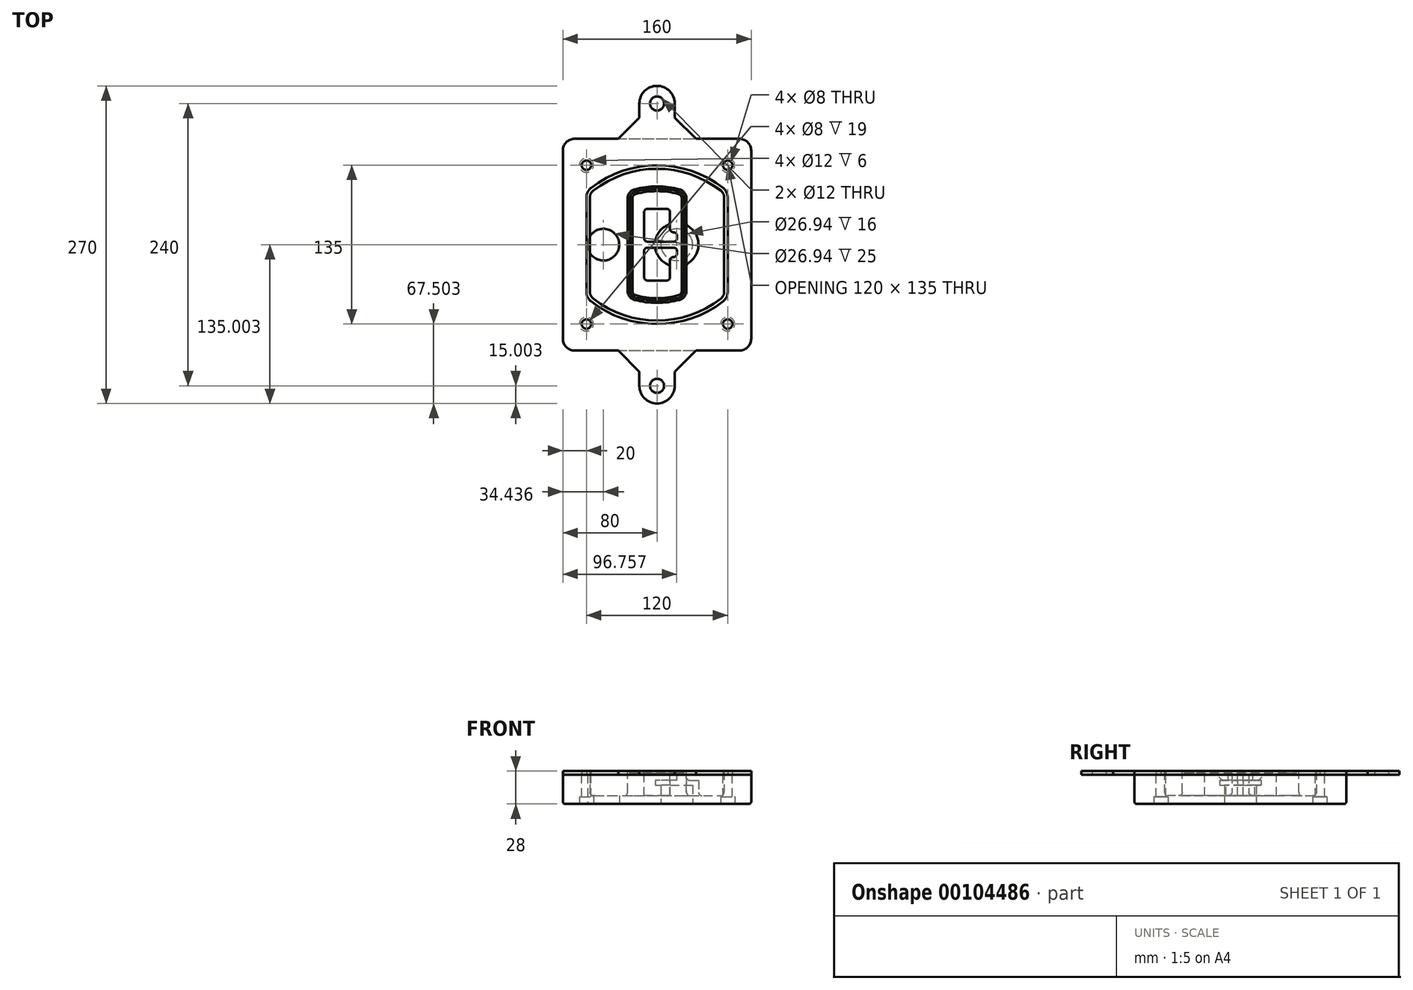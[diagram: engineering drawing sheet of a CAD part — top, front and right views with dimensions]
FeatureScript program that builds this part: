
annotation { "Feature Type Name" : "Feature", "Feature Type Description" : "" }
export const myFeature = defineFeature(function(context is Context, id is Id, definition is map)
    precondition{}
    {
        {
            var Q0;
            Q0=qCreatedBy(makeId("Top.planeOp"),FACE);
            var sketch = newSketch(context, id + "F0", { "sketchPlane" : qUnion([Q0])});
            skPoint(sketch, "E0.rect.middle", {"position": v(0, 0) * mm});
            skLineSegment(sketch, "E1.bottom", {"start": v(24.05, 28.38) * mm, "end": v(164.05, 28.38) * mm});
            skLineSegment(sketch, "E1.top", {"start": v(24.05, 208.38) * mm, "end": v(164.05, 208.38) * mm});
            skLineSegment(sketch, "E1.left", {"start": v(14.05, 38.38) * mm, "end": v(14.05, 198.38) * mm});
            skLineSegment(sketch, "E1.right", {"start": v(174.05, 38.38) * mm, "end": v(174.05, 198.38) * mm});
            skLineSegment(sketch, "E2", {"start": v(14.05, 208.38) * mm, "end": v(174.05, 28.38) * mm, "construction": true});
            skLineSegment(sketch, "E3", {"start": v(174.05, 208.38) * mm, "end": v(14.05, 28.38) * mm, "construction": true});
            skCircle(sketch, "E4", {"center": v(34.05, 185.88) * mm, "radius": 4 * mm});
            skCircle(sketch, "E5", {"center": v(154.05, 185.88) * mm, "radius": 4 * mm});
            skCircle(sketch, "E6", {"center": v(154.05, 50.88) * mm, "radius": 4 * mm});
            skCircle(sketch, "E7", {"center": v(34.05, 50.88) * mm, "radius": 4 * mm});
            skLineSegment(sketch, "E8", {"start": v(34.05, 185.88) * mm, "end": v(154.05, 185.88) * mm, "construction": true});
            skLineSegment(sketch, "E9", {"start": v(154.05, 185.88) * mm, "end": v(154.05, 50.88) * mm, "construction": true});
            skLineSegment(sketch, "E10", {"start": v(154.05, 50.88) * mm, "end": v(34.05, 50.88) * mm, "construction": true});
            skLineSegment(sketch, "E11", {"start": v(34.05, 50.88) * mm, "end": v(34.05, 185.88) * mm, "construction": true});
            skLineSegment(sketch, "E12", {"start": v(34.05, 158.68) * mm, "end": v(34.05, 78.09) * mm});
            skLineSegment(sketch, "E13", {"start": v(154.05, 158.68) * mm, "end": v(154.05, 78.09) * mm});
            skArc(sketch, "E14", {"start": v(150.2, 166.56) * mm, "mid": v(94.05, 185.88) * mm, "end": v(37.9, 166.56) * mm});
            skArc(sketch, "E15", {"start": v(37.9, 70.2) * mm, "mid": v(94.05, 50.88) * mm, "end": v(150.2, 70.2) * mm});
            skLineSegment(sketch, "E16", {"start": v(34.05, 118.38) * mm, "end": v(154.05, 118.38) * mm, "construction": true});
            skPoint(sketch, "E17.visualSharp", {"position": v(34.05, 73.38) * mm});
            skArc(sketch, "E17.filletArc", {"start": v(34.05, 78.09) * mm, "mid": v(35.06, 73.7) * mm, "end": v(37.9, 70.2) * mm});
            skPoint(sketch, "E18.visualSharp", {"position": v(34.05, 163.38) * mm});
            skArc(sketch, "E18.filletArc", {"start": v(37.9, 166.56) * mm, "mid": v(35.06, 163.06) * mm, "end": v(34.05, 158.68) * mm});
            skPoint(sketch, "E19.visualSharp", {"position": v(154.05, 163.38) * mm});
            skArc(sketch, "E19.filletArc", {"start": v(154.05, 158.68) * mm, "mid": v(153.04, 163.06) * mm, "end": v(150.2, 166.56) * mm});
            skPoint(sketch, "E20.visualSharp", {"position": v(154.05, 73.38) * mm});
            skArc(sketch, "E20.filletArc", {"start": v(150.2, 70.2) * mm, "mid": v(153.04, 73.7) * mm, "end": v(154.05, 78.09) * mm});
            skPoint(sketch, "E21.visualSharp", {"position": v(14.05, 208.38) * mm});
            skArc(sketch, "E21.filletArc", {"start": v(24.05, 208.38) * mm, "mid": v(16.98, 205.45) * mm, "end": v(14.05, 198.38) * mm});
            skPoint(sketch, "E22.visualSharp", {"position": v(174.05, 208.38) * mm});
            skArc(sketch, "E22.filletArc", {"start": v(174.05, 198.38) * mm, "mid": v(171.12, 205.45) * mm, "end": v(164.05, 208.38) * mm});
            skPoint(sketch, "E23.visualSharp", {"position": v(174.05, 28.38) * mm});
            skArc(sketch, "E23.filletArc", {"start": v(164.05, 28.38) * mm, "mid": v(171.12, 31.31) * mm, "end": v(174.05, 38.38) * mm});
            skPoint(sketch, "E24.visualSharp", {"position": v(14.05, 28.38) * mm});
            skArc(sketch, "E24.filletArc", {"start": v(14.05, 38.38) * mm, "mid": v(16.98, 31.31) * mm, "end": v(24.05, 28.38) * mm});
            skArc(sketch, "E25.0", {"start": v(151.05, 158.68) * mm, "mid": v(150.34, 161.75) * mm, "end": v(148.36, 164.2) * mm});
            skLineSegment(sketch, "E25.1", {"start": v(151.05, 158.68) * mm, "end": v(151.05, 78.09) * mm});
            skArc(sketch, "E25.2", {"start": v(148.36, 72.57) * mm, "mid": v(150.34, 75.02) * mm, "end": v(151.05, 78.09) * mm});
            skArc(sketch, "E25.3", {"start": v(39.74, 72.57) * mm, "mid": v(94.05, 53.88) * mm, "end": v(148.36, 72.57) * mm});
            skArc(sketch, "E25.4", {"start": v(37.05, 78.09) * mm, "mid": v(37.76, 75.02) * mm, "end": v(39.74, 72.57) * mm});
            skArc(sketch, "E25.5", {"start": v(148.36, 164.2) * mm, "mid": v(94.05, 182.88) * mm, "end": v(39.74, 164.2) * mm});
            skLineSegment(sketch, "E25.6", {"start": v(37.05, 158.68) * mm, "end": v(37.05, 78.09) * mm});
            skArc(sketch, "E25.7", {"start": v(39.74, 164.2) * mm, "mid": v(37.76, 161.75) * mm, "end": v(37.05, 158.68) * mm});
            skArc(sketch, "E26.0", {"start": v(35.43, 169.71) * mm, "mid": v(31.47, 164.82) * mm, "end": v(30.05, 158.68) * mm});
            skArc(sketch, "E26.1", {"start": v(152.67, 169.71) * mm, "mid": v(94.05, 189.88) * mm, "end": v(35.43, 169.71) * mm});
            skArc(sketch, "E26.2", {"start": v(158.05, 158.68) * mm, "mid": v(156.63, 164.82) * mm, "end": v(152.67, 169.71) * mm});
            skLineSegment(sketch, "E26.3", {"start": v(158.05, 158.68) * mm, "end": v(158.05, 78.09) * mm});
            skArc(sketch, "E26.4", {"start": v(152.67, 67.05) * mm, "mid": v(156.63, 71.95) * mm, "end": v(158.05, 78.09) * mm});
            skLineSegment(sketch, "E26.5", {"start": v(30.05, 158.68) * mm, "end": v(30.05, 78.09) * mm});
            skArc(sketch, "E26.6", {"start": v(35.43, 67.05) * mm, "mid": v(94.05, 46.88) * mm, "end": v(152.67, 67.05) * mm});
            skArc(sketch, "E26.7", {"start": v(30.05, 78.09) * mm, "mid": v(31.47, 71.95) * mm, "end": v(35.43, 67.05) * mm});
            skSolve(sketch);
        }
        {
            var Q0;
            Q0=makeQuery(id+"F0.imprint","IMPRINT",FACE,{"disambiguationData":[TD([[makeQuery(id+"F0.imprint","IMPRINT",EDGE,{"derivedFrom":sQuery(id+"F0.wireOp",EDGE,"E1.bottom")}),1.0]])]});
            var Q1;
            Q1=makeQuery(id+"F0.imprint","IMPRINT",FACE,{"disambiguationData":[TD([[makeQuery(id+"F0.imprint","IMPRINT",EDGE,{"derivedFrom":sQuery(id+"F0.wireOp",EDGE,"E12")}),1.0]])]});
            var Q2;
            Q2=makeQuery(id+"F0.imprint","IMPRINT",FACE,{"disambiguationData":[TD([[makeQuery(id+"F0.imprint","IMPRINT",EDGE,{"derivedFrom":sQuery(id+"F0.wireOp",EDGE,"E25.0")}),1.0]])]});
            var Q3;
            Q3=makeQuery(id+"F0.imprint","IMPRINT",FACE,{"disambiguationData":[TD([[makeQuery(id+"F0.imprint","IMPRINT",EDGE,{"derivedFrom":sQuery(id+"F0.wireOp",EDGE,"E12")}),-1.0]])]});
            extrude(context, id + "F1", {"entities" : qUnion([Q0, Q1, Q2, Q3]), "oppositeDirection" : true, "depth" : 25 * mm});
        }
        {
            var Q0;
            Q0=makeQuery(id+"F0.imprint","IMPRINT",FACE,{"disambiguationData":[TD([[makeQuery(id+"F0.imprint","IMPRINT",EDGE,{"derivedFrom":sQuery(id+"F0.wireOp",EDGE,"E12")}),1.0]])]});
            extrude(context, id + "F2", {"entities" : qUnion([Q0]), "operationType" : NewBodyOperationType.ADD, "depth" : 3 * mm});
        }
        {
            var Q0;
            Q0=makeQuery(id+"F0.imprint","IMPRINT",FACE,{"disambiguationData":[TD([[makeQuery(id+"F0.imprint","IMPRINT",EDGE,{"derivedFrom":sQuery(id+"F0.wireOp",EDGE,"E25.0")}),1.0]])]});
            extrude(context, id + "F3", {"entities" : qUnion([Q0]), "operationType" : NewBodyOperationType.REMOVE, "oppositeDirection" : true, "depth" : 18 * mm});
        }
        {
            var Q0;
            Q0=makeQuery(id+"F2.opExtrude","CAP_FACE",FACE,{"disambiguationData":[OSD([sQuery(id+"F0.wireOp",EDGE,"E12"),sQuery(id+"F0.wireOp",EDGE,"E13"),sQuery(id+"F0.wireOp",EDGE,"E14"),sQuery(id+"F0.wireOp",EDGE,"E15"),sQuery(id+"F0.wireOp",EDGE,"E17.filletArc"),sQuery(id+"F0.wireOp",EDGE,"E18.filletArc"),sQuery(id+"F0.wireOp",EDGE,"E19.filletArc"),sQuery(id+"F0.wireOp",EDGE,"E20.filletArc"),sQuery(id+"F0.wireOp",EDGE,"E25.0"),sQuery(id+"F0.wireOp",EDGE,"E25.1"),sQuery(id+"F0.wireOp",EDGE,"E25.2"),sQuery(id+"F0.wireOp",EDGE,"E25.3"),sQuery(id+"F0.wireOp",EDGE,"E25.4"),sQuery(id+"F0.wireOp",EDGE,"E25.5"),sQuery(id+"F0.wireOp",EDGE,"E25.6"),sQuery(id+"F0.wireOp",EDGE,"E25.7")])],"isStart":false});
            var sketch = newSketch(context, id + "F4", { "sketchPlane" : qUnion([Q0])});
            skArc(sketch, "E27.0", {"start": v(74.97, 71.41) * mm, "mid": v(94.05, 68.88) * mm, "end": v(113.13, 71.41) * mm});
            skArc(sketch, "E28.0", {"start": v(113.13, 165.35) * mm, "mid": v(94.05, 167.88) * mm, "end": v(74.97, 165.35) * mm});
            skLineSegment(sketch, "E29", {"start": v(69.05, 157.63) * mm, "end": v(69.05, 79.14) * mm});
            skLineSegment(sketch, "E30", {"start": v(119.05, 157.63) * mm, "end": v(119.05, 79.14) * mm});
            skLineSegment(sketch, "E31", {"start": v(69.05, 163.48) * mm, "end": v(119.05, 163.48) * mm, "construction": true});
            skLineSegment(sketch, "E32", {"start": v(69.05, 73.28) * mm, "end": v(119.05, 73.28) * mm, "construction": true});
            skPoint(sketch, "E33.visualSharp", {"position": v(69.05, 163.48) * mm});
            skArc(sketch, "E33.filletArc", {"start": v(74.97, 165.35) * mm, "mid": v(70.7, 162.5) * mm, "end": v(69.05, 157.63) * mm});
            skPoint(sketch, "E34.visualSharp", {"position": v(119.05, 163.48) * mm});
            skArc(sketch, "E34.filletArc", {"start": v(119.05, 157.63) * mm, "mid": v(117.4, 162.5) * mm, "end": v(113.13, 165.35) * mm});
            skPoint(sketch, "E35.visualSharp", {"position": v(119.05, 73.28) * mm});
            skArc(sketch, "E35.filletArc", {"start": v(113.13, 71.41) * mm, "mid": v(117.4, 74.27) * mm, "end": v(119.05, 79.14) * mm});
            skPoint(sketch, "E36.visualSharp", {"position": v(69.05, 73.28) * mm});
            skArc(sketch, "E36.filletArc", {"start": v(69.05, 79.14) * mm, "mid": v(70.7, 74.27) * mm, "end": v(74.97, 71.41) * mm});
            skArc(sketch, "E37.0", {"start": v(148.36, 164.2) * mm, "mid": v(94.05, 182.88) * mm, "end": v(39.74, 164.2) * mm});
            skArc(sketch, "E37.1", {"start": v(39.74, 164.2) * mm, "mid": v(37.76, 161.75) * mm, "end": v(37.05, 158.68) * mm});
            skLineSegment(sketch, "E37.2", {"start": v(37.05, 158.68) * mm, "end": v(37.05, 78.09) * mm});
            skArc(sketch, "E37.3", {"start": v(37.05, 78.09) * mm, "mid": v(37.76, 75.02) * mm, "end": v(39.74, 72.57) * mm});
            skArc(sketch, "E37.4", {"start": v(39.74, 72.57) * mm, "mid": v(94.05, 53.88) * mm, "end": v(148.36, 72.57) * mm});
            skArc(sketch, "E37.5", {"start": v(148.36, 72.57) * mm, "mid": v(150.34, 75.02) * mm, "end": v(151.05, 78.09) * mm});
            skLineSegment(sketch, "E37.6", {"start": v(151.05, 158.68) * mm, "end": v(151.05, 78.09) * mm});
            skArc(sketch, "E37.7", {"start": v(151.05, 158.68) * mm, "mid": v(150.34, 161.75) * mm, "end": v(148.36, 164.2) * mm});
            skLineSegment(sketch, "E38.0", {"start": v(117.05, 157.63) * mm, "end": v(117.05, 79.14) * mm});
            skArc(sketch, "E38.1", {"start": v(112.61, 73.34) * mm, "mid": v(115.81, 75.49) * mm, "end": v(117.05, 79.14) * mm});
            skArc(sketch, "E38.2", {"start": v(75.49, 73.34) * mm, "mid": v(94.05, 70.88) * mm, "end": v(112.61, 73.34) * mm});
            skArc(sketch, "E38.3", {"start": v(71.05, 79.14) * mm, "mid": v(72.29, 75.49) * mm, "end": v(75.49, 73.34) * mm});
            skLineSegment(sketch, "E38.4", {"start": v(71.05, 157.63) * mm, "end": v(71.05, 79.14) * mm});
            skArc(sketch, "E38.5", {"start": v(117.05, 157.63) * mm, "mid": v(115.81, 161.28) * mm, "end": v(112.61, 163.42) * mm});
            skArc(sketch, "E38.6", {"start": v(75.49, 163.42) * mm, "mid": v(72.29, 161.28) * mm, "end": v(71.05, 157.63) * mm});
            skArc(sketch, "E38.7", {"start": v(112.61, 163.42) * mm, "mid": v(94.05, 165.88) * mm, "end": v(75.49, 163.42) * mm});
            skArc(sketch, "E39.0", {"start": v(115.05, 157.63) * mm, "mid": v(114.23, 160.06) * mm, "end": v(112.1, 161.5) * mm});
            skLineSegment(sketch, "E39.1", {"start": v(115.05, 157.63) * mm, "end": v(115.05, 79.14) * mm});
            skArc(sketch, "E39.2", {"start": v(112.1, 75.27) * mm, "mid": v(114.23, 76.7) * mm, "end": v(115.05, 79.14) * mm});
            skArc(sketch, "E39.3", {"start": v(76, 75.27) * mm, "mid": v(94.05, 72.88) * mm, "end": v(112.1, 75.27) * mm});
            skArc(sketch, "E39.4", {"start": v(73.05, 79.14) * mm, "mid": v(73.87, 76.7) * mm, "end": v(76, 75.27) * mm});
            skArc(sketch, "E39.5", {"start": v(112.1, 161.5) * mm, "mid": v(94.05, 163.88) * mm, "end": v(76, 161.5) * mm});
            skLineSegment(sketch, "E39.6", {"start": v(73.05, 157.63) * mm, "end": v(73.05, 79.14) * mm});
            skArc(sketch, "E39.7", {"start": v(76, 161.5) * mm, "mid": v(73.87, 160.06) * mm, "end": v(73.05, 157.63) * mm});
            skLineSegment(sketch, "E40", {"start": v(69.05, 118.38) * mm, "end": v(119.05, 118.38) * mm, "construction": true});
            skLineSegment(sketch, "E41", {"start": v(83.05, 123.88) * mm, "end": v(83.05, 145.88) * mm});
            skLineSegment(sketch, "E42", {"start": v(86.05, 148.88) * mm, "end": v(102.05, 148.88) * mm});
            skLineSegment(sketch, "E43", {"start": v(105.05, 145.88) * mm, "end": v(105.05, 131.88) * mm});
            skLineSegment(sketch, "E44", {"start": v(108.05, 128.88) * mm, "end": v(108.05, 128.88) * mm});
            skLineSegment(sketch, "E45", {"start": v(111.05, 125.88) * mm, "end": v(111.05, 123.88) * mm});
            skLineSegment(sketch, "E46", {"start": v(108.05, 120.88) * mm, "end": v(86.05, 120.88) * mm});
            skPoint(sketch, "E47.visualSharp", {"position": v(83.05, 148.88) * mm});
            skArc(sketch, "E47.filletArc", {"start": v(86.05, 148.88) * mm, "mid": v(83.93, 148) * mm, "end": v(83.05, 145.88) * mm});
            skPoint(sketch, "E48.visualSharp", {"position": v(105.05, 148.88) * mm});
            skArc(sketch, "E48.filletArc", {"start": v(105.05, 145.88) * mm, "mid": v(104.17, 148) * mm, "end": v(102.05, 148.88) * mm});
            skPoint(sketch, "E49.visualSharp", {"position": v(105.05, 128.88) * mm});
            skArc(sketch, "E49.filletArc", {"start": v(105.05, 131.88) * mm, "mid": v(105.93, 129.76) * mm, "end": v(108.05, 128.88) * mm});
            skPoint(sketch, "E50.visualSharp", {"position": v(111.05, 128.88) * mm});
            skArc(sketch, "E50.filletArc", {"start": v(111.05, 125.88) * mm, "mid": v(110.17, 128) * mm, "end": v(108.05, 128.88) * mm});
            skPoint(sketch, "E51.visualSharp", {"position": v(111.05, 120.88) * mm});
            skArc(sketch, "E51.filletArc", {"start": v(108.05, 120.88) * mm, "mid": v(110.17, 121.76) * mm, "end": v(111.05, 123.88) * mm});
            skPoint(sketch, "E52.visualSharp", {"position": v(83.05, 120.88) * mm});
            skArc(sketch, "E52.filletArc", {"start": v(83.05, 123.88) * mm, "mid": v(83.93, 121.76) * mm, "end": v(86.05, 120.88) * mm});
            skLineSegment(sketch, "E53.0.MirrorCS", {"start": v(108.05, 115.88) * mm, "end": v(86.05, 115.88) * mm});
            skArc(sketch, "E54.0.MirrorCS", {"start": v(83.05, 112.88) * mm, "mid": v(83.93, 115) * mm, "end": v(86.05, 115.88) * mm});
            skLineSegment(sketch, "E55.0.MirrorCS", {"start": v(83.05, 112.88) * mm, "end": v(83.05, 90.88) * mm});
            skArc(sketch, "E56.0.MirrorCS", {"start": v(86.05, 87.88) * mm, "mid": v(83.93, 88.76) * mm, "end": v(83.05, 90.88) * mm});
            skLineSegment(sketch, "E57.0.MirrorCS", {"start": v(86.05, 87.88) * mm, "end": v(102.05, 87.88) * mm});
            skArc(sketch, "E58.0.MirrorCS", {"start": v(105.05, 90.88) * mm, "mid": v(104.17, 88.76) * mm, "end": v(102.05, 87.88) * mm});
            skLineSegment(sketch, "E59.0.MirrorCS", {"start": v(105.05, 90.88) * mm, "end": v(105.05, 104.88) * mm});
            skArc(sketch, "E60.0.MirrorCS", {"start": v(105.05, 104.88) * mm, "mid": v(105.93, 107) * mm, "end": v(108.05, 107.88) * mm});
            skArc(sketch, "E61.0.MirrorCS", {"start": v(111.05, 110.88) * mm, "mid": v(110.17, 108.76) * mm, "end": v(108.05, 107.88) * mm});
            skLineSegment(sketch, "E62.0.MirrorCS", {"start": v(111.05, 110.88) * mm, "end": v(111.05, 112.88) * mm});
            skArc(sketch, "E63.0.MirrorCS", {"start": v(108.05, 115.88) * mm, "mid": v(110.17, 115) * mm, "end": v(111.05, 112.88) * mm});
            skSolve(sketch);
        }
        {
            var Q0;
            Q0=makeQuery(id+"F4.imprint","IMPRINT",FACE,{"disambiguationData":[TD([[makeQuery(id+"F4.imprint","IMPRINT",EDGE,{"derivedFrom":sQuery(id+"F4.wireOp",EDGE,"E27.0")}),1.0]])]});
            var Q1;
            Q1=makeQuery(id+"F4.imprint","IMPRINT",FACE,{"disambiguationData":[TD([[makeQuery(id+"F4.imprint","IMPRINT",EDGE,{"derivedFrom":sQuery(id+"F4.wireOp",EDGE,"E38.0")}),-1.0]])]});
            var Q2;
            Q2=makeQuery(id+"F4.imprint","IMPRINT",FACE,{"disambiguationData":[TD([[makeQuery(id+"F4.imprint","IMPRINT",EDGE,{"derivedFrom":sQuery(id+"F4.wireOp",EDGE,"E39.0")}),1.0]])]});
            extrude(context, id + "F5", {"entities" : qUnion([Q0, Q1, Q2]), "operationType" : NewBodyOperationType.ADD, "endBound" : BoundingType.UP_TO_NEXT, "oppositeDirection" : true, "depth" : 25 * mm});
        }
        {
            var Q0;
            Q0=makeQuery(id+"F4.imprint","IMPRINT",FACE,{"disambiguationData":[TD([[makeQuery(id+"F4.imprint","IMPRINT",EDGE,{"derivedFrom":sQuery(id+"F4.wireOp",EDGE,"E38.0")}),-1.0]])]});
            extrude(context, id + "F6", {"entities" : qUnion([Q0]), "operationType" : NewBodyOperationType.REMOVE, "oppositeDirection" : true, "depth" : 2 * mm});
        }
        {
            var Q0;
            Q0=makeQuery(id+"F1.opExtrude","CAP_FACE",FACE,{"disambiguationData":[OSD([sQuery(id+"F0.wireOp",EDGE,"E1.bottom"),sQuery(id+"F0.wireOp",EDGE,"E1.top"),sQuery(id+"F0.wireOp",EDGE,"E1.left"),sQuery(id+"F0.wireOp",EDGE,"E1.right"),sQuery(id+"F0.wireOp",EDGE,"E4"),sQuery(id+"F0.wireOp",EDGE,"E5"),sQuery(id+"F0.wireOp",EDGE,"E6"),sQuery(id+"F0.wireOp",EDGE,"E7"),sQuery(id+"F0.wireOp",EDGE,"E21.filletArc"),sQuery(id+"F0.wireOp",EDGE,"E22.filletArc"),sQuery(id+"F0.wireOp",EDGE,"E23.filletArc"),sQuery(id+"F0.wireOp",EDGE,"E24.filletArc")])],"isStart":false});
            var sketch = newSketch(context, id + "F7", { "sketchPlane" : qUnion([Q0])});
            skCircle(sketch, "E64", {"center": v(110.8, -118.38) * mm, "radius": 13.47 * mm});
            skCircle(sketch, "E65", {"center": v(48.49, -118.38) * mm, "radius": 13.47 * mm});
            skLineSegment(sketch, "E66", {"start": v(174.05, -118.38) * mm, "end": v(14.05, -118.38) * mm});
            skCircle(sketch, "E67", {"center": v(110.8, -118.38) * mm, "radius": 18.47 * mm});
            skCircle(sketch, "E68", {"center": v(154.05, -185.88) * mm, "radius": 6 * mm});
            skCircle(sketch, "E69", {"center": v(34.05, -185.88) * mm, "radius": 6 * mm});
            skCircle(sketch, "E70", {"center": v(34.05, -50.88) * mm, "radius": 6 * mm});
            skCircle(sketch, "E71", {"center": v(154.05, -50.88) * mm, "radius": 6 * mm});
            skSolve(sketch);
        }
        {
            var Q0;
            {var subQ1=sQuery(id+"F7.wireOp",EDGE,"E66");var subQ4=sQuery(id+"F7.wireOp",EDGE,"E64");var subQ6=makeQuery(id+"F7.imprint","INTERSECT",VERTEX,{"disambiguationData":[OD(0.0)],"derivedFrom":[subQ4,subQ1]});Q0=makeQuery(id+"F7.imprint","IMPRINT",FACE,{"disambiguationData":[TD([[makeQuery(id+"F7.imprint","IMPRINT",EDGE,{"disambiguationData":[TD([[subQ6,-1.0]])],"derivedFrom":subQ4}),-1.0]])]});}
            var Q1;
            {var subQ0=sQuery(id+"F7.wireOp",EDGE,"E66");var subQ1=sQuery(id+"F7.wireOp",EDGE,"E64");var subQ3=makeQuery(id+"F7.imprint","INTERSECT",VERTEX,{"disambiguationData":[OD(0.0)],"derivedFrom":[subQ1,subQ0]});Q1=makeQuery(id+"F7.imprint","IMPRINT",FACE,{"disambiguationData":[TD([[makeQuery(id+"F7.imprint","IMPRINT",EDGE,{"disambiguationData":[TD([[subQ3,-1.0]])],"derivedFrom":subQ1}),1.0]])]});}
            var Q2;
            {var subQ0=sQuery(id+"F7.wireOp",EDGE,"E66");var subQ1=sQuery(id+"F7.wireOp",EDGE,"E64");var subQ3=makeQuery(id+"F7.imprint","INTERSECT",VERTEX,{"disambiguationData":[OD(0.0)],"derivedFrom":[subQ1,subQ0]});Q2=makeQuery(id+"F7.imprint","IMPRINT",FACE,{"disambiguationData":[TD([[makeQuery(id+"F7.imprint","IMPRINT",EDGE,{"disambiguationData":[TD([[subQ3,1.0]])],"derivedFrom":subQ1}),1.0]])]});}
            var Q3;
            {var subQ1=sQuery(id+"F7.wireOp",EDGE,"E66");var subQ4=sQuery(id+"F7.wireOp",EDGE,"E64");var subQ6=makeQuery(id+"F7.imprint","INTERSECT",VERTEX,{"disambiguationData":[OD(0.0)],"derivedFrom":[subQ4,subQ1]});Q3=makeQuery(id+"F7.imprint","IMPRINT",FACE,{"disambiguationData":[TD([[makeQuery(id+"F7.imprint","IMPRINT",EDGE,{"disambiguationData":[TD([[subQ6,1.0]])],"derivedFrom":subQ4}),-1.0]])]});}
            extrude(context, id + "F8", {"entities" : qUnion([Q0, Q1, Q2, Q3]), "operationType" : NewBodyOperationType.ADD, "oppositeDirection" : true, "depth" : 20 * mm});
        }
        {
            var Q0;
            {var subQ0=sQuery(id+"F7.wireOp",EDGE,"E66");var subQ1=sQuery(id+"F7.wireOp",EDGE,"E64");var subQ3=makeQuery(id+"F7.imprint","INTERSECT",VERTEX,{"disambiguationData":[OD(0.0)],"derivedFrom":[subQ1,subQ0]});Q0=makeQuery(id+"F7.imprint","IMPRINT",FACE,{"disambiguationData":[TD([[makeQuery(id+"F7.imprint","IMPRINT",EDGE,{"disambiguationData":[TD([[subQ3,-1.0]])],"derivedFrom":subQ1}),1.0]])]});}
            var Q1;
            {var subQ0=sQuery(id+"F7.wireOp",EDGE,"E66");var subQ1=sQuery(id+"F7.wireOp",EDGE,"E64");var subQ3=makeQuery(id+"F7.imprint","INTERSECT",VERTEX,{"disambiguationData":[OD(0.0)],"derivedFrom":[subQ1,subQ0]});Q1=makeQuery(id+"F7.imprint","IMPRINT",FACE,{"disambiguationData":[TD([[makeQuery(id+"F7.imprint","IMPRINT",EDGE,{"disambiguationData":[TD([[subQ3,1.0]])],"derivedFrom":subQ1}),1.0]])]});}
            extrude(context, id + "F9", {"entities" : qUnion([Q0, Q1]), "operationType" : NewBodyOperationType.REMOVE, "oppositeDirection" : true, "depth" : 16 * mm});
        }
        {
            var Q0;
            {var subQ0=sQuery(id+"F7.wireOp",EDGE,"E66");var subQ1=sQuery(id+"F7.wireOp",EDGE,"E65");var subQ3=makeQuery(id+"F7.imprint","INTERSECT",VERTEX,{"disambiguationData":[OD(0.0)],"derivedFrom":[subQ1,subQ0]});Q0=makeQuery(id+"F7.imprint","IMPRINT",FACE,{"disambiguationData":[TD([[makeQuery(id+"F7.imprint","IMPRINT",EDGE,{"disambiguationData":[TD([[subQ3,-1.0]])],"derivedFrom":subQ1}),1.0]])]});}
            var Q1;
            {var subQ0=sQuery(id+"F7.wireOp",EDGE,"E66");var subQ1=sQuery(id+"F7.wireOp",EDGE,"E65");var subQ3=makeQuery(id+"F7.imprint","INTERSECT",VERTEX,{"disambiguationData":[OD(0.0)],"derivedFrom":[subQ1,subQ0]});Q1=makeQuery(id+"F7.imprint","IMPRINT",FACE,{"disambiguationData":[TD([[makeQuery(id+"F7.imprint","IMPRINT",EDGE,{"disambiguationData":[TD([[subQ3,1.0]])],"derivedFrom":subQ1}),1.0]])]});}
            extrude(context, id + "F10", {"entities" : qUnion([Q0, Q1]), "operationType" : NewBodyOperationType.REMOVE, "oppositeDirection" : true, "depth" : 25 * mm});
        }
        {
            var Q0;
            Q0=makeQuery(id+"F7.imprint","IMPRINT",FACE,{"disambiguationData":[TD([[makeQuery(id+"F7.imprint","IMPRINT",EDGE,{"derivedFrom":sQuery(id+"F7.wireOp",EDGE,"E68")}),1.0]])]});
            var Q1;
            Q1=makeQuery(id+"F7.imprint","IMPRINT",FACE,{"disambiguationData":[TD([[makeQuery(id+"F7.imprint","IMPRINT",EDGE,{"derivedFrom":makeQuery(id+"F1.opExtrude","CAP_EDGE",EDGE,{"disambiguationData":[OSD([sQuery(id+"F0.wireOp",EDGE,"E5")])],"isStart":false})}),-1.0]])]});
            var Q2;
            Q2=makeQuery(id+"F7.imprint","IMPRINT",FACE,{"disambiguationData":[TD([[makeQuery(id+"F7.imprint","IMPRINT",EDGE,{"derivedFrom":sQuery(id+"F7.wireOp",EDGE,"E69")}),1.0]])]});
            var Q3;
            Q3=makeQuery(id+"F7.imprint","IMPRINT",FACE,{"disambiguationData":[TD([[makeQuery(id+"F7.imprint","IMPRINT",EDGE,{"derivedFrom":makeQuery(id+"F1.opExtrude","CAP_EDGE",EDGE,{"disambiguationData":[OSD([sQuery(id+"F0.wireOp",EDGE,"E4")])],"isStart":false})}),-1.0]])]});
            var Q4;
            Q4=makeQuery(id+"F7.imprint","IMPRINT",FACE,{"disambiguationData":[TD([[makeQuery(id+"F7.imprint","IMPRINT",EDGE,{"derivedFrom":sQuery(id+"F7.wireOp",EDGE,"E70")}),1.0]])]});
            var Q5;
            Q5=makeQuery(id+"F7.imprint","IMPRINT",FACE,{"disambiguationData":[TD([[makeQuery(id+"F7.imprint","IMPRINT",EDGE,{"derivedFrom":makeQuery(id+"F1.opExtrude","CAP_EDGE",EDGE,{"disambiguationData":[OSD([sQuery(id+"F0.wireOp",EDGE,"E7")])],"isStart":false})}),-1.0]])]});
            var Q6;
            Q6=makeQuery(id+"F7.imprint","IMPRINT",FACE,{"disambiguationData":[TD([[makeQuery(id+"F7.imprint","IMPRINT",EDGE,{"derivedFrom":sQuery(id+"F7.wireOp",EDGE,"E71")}),1.0]])]});
            var Q7;
            Q7=makeQuery(id+"F7.imprint","IMPRINT",FACE,{"disambiguationData":[TD([[makeQuery(id+"F7.imprint","IMPRINT",EDGE,{"derivedFrom":makeQuery(id+"F1.opExtrude","CAP_EDGE",EDGE,{"disambiguationData":[OSD([sQuery(id+"F0.wireOp",EDGE,"E6")])],"isStart":false})}),-1.0]])]});
            extrude(context, id + "F11", {"entities" : qUnion([Q0, Q1, Q2, Q3, Q4, Q5, Q6, Q7]), "operationType" : NewBodyOperationType.REMOVE, "oppositeDirection" : true, "depth" : 6 * mm});
        }
        {
            var Q0;
            Q0=makeQuery(id+"F9.boolean.opBoolean","COPY",FACE,{"derivedFrom":makeQuery(id+"F9.opExtrude","CAP_FACE",FACE,{"disambiguationData":[OSD([sQuery(id+"F7.wireOp",EDGE,"E64")])],"isStart":false})});
            var sketch = newSketch(context, id + "F12", { "sketchPlane" : qUnion([Q0])});
            skArc(sketch, "E72.0", {"start": v(105.05, -100.83) * mm, "mid": v(96.62, -106.56) * mm, "end": v(92.5, -115.88) * mm});
            skArc(sketch, "E72.1", {"start": v(92.5, -120.88) * mm, "mid": v(96.62, -130.2) * mm, "end": v(105.05, -135.93) * mm});
            skLineSegment(sketch, "E73", {"start": v(92.5, -120.88) * mm, "end": v(108.05, -120.88) * mm});
            skLineSegment(sketch, "E74.0", {"start": v(108.05, -115.88) * mm, "end": v(92.5, -115.88) * mm});
            skArc(sketch, "E74.1", {"start": v(108.05, -115.88) * mm, "mid": v(110.17, -115) * mm, "end": v(111.05, -112.88) * mm});
            skLineSegment(sketch, "E74.2", {"start": v(111.05, -110.88) * mm, "end": v(111.05, -112.88) * mm});
            skArc(sketch, "E74.3", {"start": v(111.05, -110.88) * mm, "mid": v(110.17, -108.76) * mm, "end": v(108.05, -107.88) * mm});
            skArc(sketch, "E74.4", {"start": v(105.05, -104.88) * mm, "mid": v(105.93, -107) * mm, "end": v(108.05, -107.88) * mm});
            skLineSegment(sketch, "E74.5", {"start": v(105.05, -100.83) * mm, "end": v(105.05, -104.88) * mm});
            skLineSegment(sketch, "E74.7", {"start": v(108.05, -120.88) * mm, "end": v(92.5, -120.88) * mm});
            skArc(sketch, "E74.8", {"start": v(108.05, -120.88) * mm, "mid": v(110.17, -121.76) * mm, "end": v(111.05, -123.88) * mm});
            skLineSegment(sketch, "E74.9", {"start": v(111.05, -125.88) * mm, "end": v(111.05, -123.88) * mm});
            skArc(sketch, "E74.10", {"start": v(111.05, -125.88) * mm, "mid": v(110.17, -128) * mm, "end": v(108.05, -128.88) * mm});
            skArc(sketch, "E74.11", {"start": v(105.05, -131.88) * mm, "mid": v(105.93, -129.76) * mm, "end": v(108.05, -128.88) * mm});
            skLineSegment(sketch, "E74.12", {"start": v(105.05, -135.93) * mm, "end": v(105.05, -131.88) * mm});
            skPoint(sketch, "E75.orphan", {"position": v(105.05, -145.88) * mm});
            skPoint(sketch, "E76.orphan", {"position": v(86.05, -120.88) * mm});
            skPoint(sketch, "E77.orphan", {"position": v(86.05, -115.88) * mm});
            skPoint(sketch, "E78.orphan", {"position": v(105.05, -90.88) * mm});
            skSolve(sketch);
        }
        {
            var Q0;
            {var subQ7=sQuery(id+"F12.wireOp",EDGE,"E72.0");var subQ14=sQuery(id+"F12.wireOp",EDGE,"E72.1");var subQ16=sQuery(id+"F12.wireOp",EDGE,"E74.1");var subQ18=sQuery(id+"F12.wireOp",EDGE,"E74.8");Q0=qUnion([makeQuery(id+"F12.imprint","IMPRINT",FACE,{"disambiguationData":[TD([[makeQuery(id+"F12.imprint","IMPRINT",EDGE,{"derivedFrom":subQ7}),1.0]])]}),makeQuery(id+"F12.imprint","IMPRINT",FACE,{"disambiguationData":[TD([[makeQuery(id+"F12.imprint","IMPRINT",EDGE,{"derivedFrom":subQ14}),1.0]])]}),makeQuery(id+"F12.imprint","IMPRINT",FACE,{"disambiguationData":[TD([[makeQuery(id+"F12.imprint","IMPRINT",EDGE,{"derivedFrom":subQ16}),1.0]])]}),makeQuery(id+"F12.imprint","IMPRINT",FACE,{"disambiguationData":[TD([[makeQuery(id+"F12.imprint","IMPRINT",EDGE,{"derivedFrom":subQ18}),-1.0]])]})]);}
            var Q1;
            Q1=makeQuery(id+"F5.boolean.opBoolean","SPLIT",FACE,{"disambiguationData":[TD([makeQuery(id+"F5.opExtrude","SWEPT_FACE",FACE,{"disambiguationData":[OSD([sQuery(id+"F4.wireOp",EDGE,"E41")])]})])],"derivedFrom":makeQuery(id+"F3.boolean.opBoolean","COPY",FACE,{"derivedFrom":makeQuery(id+"F3.opExtrude","CAP_FACE",FACE,{"disambiguationData":[OSD([sQuery(id+"F0.wireOp",EDGE,"E25.0"),sQuery(id+"F0.wireOp",EDGE,"E25.1"),sQuery(id+"F0.wireOp",EDGE,"E25.2"),sQuery(id+"F0.wireOp",EDGE,"E25.3"),sQuery(id+"F0.wireOp",EDGE,"E25.4"),sQuery(id+"F0.wireOp",EDGE,"E25.5"),sQuery(id+"F0.wireOp",EDGE,"E25.6"),sQuery(id+"F0.wireOp",EDGE,"E25.7")])],"isStart":false})})});
            extrude(context, id + "F13", {"entities" : qUnion([Q0]), "operationType" : NewBodyOperationType.REMOVE, "endBound" : BoundingType.UP_TO_SURFACE, "endBoundEntityFace" : qUnion([Q1]), "depth" : 25 * mm});
        }
        {
            var Q0;
            Q0=makeQuery(id+"F3.boolean.opBoolean","COPY",EDGE,{"derivedFrom":makeQuery(id+"F3.opExtrude","CAP_EDGE",EDGE,{"disambiguationData":[OSD([sQuery(id+"F0.wireOp",EDGE,"E25.6")])],"isStart":false})});
            var Q1;
            Q1=makeQuery(id+"F8.boolean.opBoolean","INTERSECT",EDGE,{"derivedFrom":[makeQuery(id+"F5.opExtrude","SWEPT_FACE",FACE,{"disambiguationData":[OSD([sQuery(id+"F4.wireOp",EDGE,"E30")])]}),makeQuery(id+"F8.opExtrude","CAP_FACE",FACE,{"disambiguationData":[OSD([sQuery(id+"F7.wireOp",EDGE,"E67")])],"isStart":false})]});
            var Q2;
            Q2=makeQuery(id+"F8.boolean.opBoolean","INTERSECT",EDGE,{"disambiguationData":[OD(1.0)],"derivedFrom":[makeQuery(id+"F5.opExtrude","SWEPT_FACE",FACE,{"disambiguationData":[OSD([sQuery(id+"F4.wireOp",EDGE,"E30")])]}),makeQuery(id+"F8.opExtrude","SWEPT_FACE",FACE,{"disambiguationData":[OSD([sQuery(id+"F7.wireOp",EDGE,"E67")])]})]});
            var Q3;
            {var subQ0=sQuery(id+"F4.wireOp",EDGE,"E30");Q3=makeQuery(id+"F8.boolean.opBoolean","SPLIT",EDGE,{"disambiguationData":[TD([makeQuery(id+"F5.opExtrude","SWEPT_FACE",FACE,{"disambiguationData":[OSD([sQuery(id+"F4.wireOp",EDGE,"E35.filletArc")])]})])],"derivedFrom":makeQuery(id+"F5.opExtrude","CAP_EDGE",EDGE,{"disambiguationData":[OSD([subQ0])],"isStart":false})});}
            var Q4;
            {var subQ0=sQuery(id+"F0.wireOp",EDGE,"E25.7");var subQ1=sQuery(id+"F0.wireOp",EDGE,"E25.1");var subQ2=sQuery(id+"F0.wireOp",EDGE,"E25.6");var subQ3=sQuery(id+"F0.wireOp",EDGE,"E25.5");var subQ4=sQuery(id+"F0.wireOp",EDGE,"E25.4");var subQ5=sQuery(id+"F0.wireOp",EDGE,"E25.0");var subQ6=sQuery(id+"F0.wireOp",EDGE,"E25.2");var subQ7=sQuery(id+"F0.wireOp",EDGE,"E25.3");Q4=makeQuery(id+"F8.boolean.opBoolean","INTERSECT",EDGE,{"derivedFrom":[makeQuery(id+"F5.boolean.opBoolean","SPLIT",FACE,{"disambiguationData":[TD([makeQuery(id+"F2.opExtrude","SWEPT_FACE",FACE,{"disambiguationData":[OSD([subQ5])]})])],"derivedFrom":makeQuery(id+"F3.boolean.opBoolean","COPY",FACE,{"derivedFrom":makeQuery(id+"F3.opExtrude","CAP_FACE",FACE,{"disambiguationData":[OSD([subQ5,subQ1,subQ6,subQ7,subQ4,subQ3,subQ2,subQ0])],"isStart":false})})}),makeQuery(id+"F8.opExtrude","SWEPT_FACE",FACE,{"disambiguationData":[OSD([sQuery(id+"F7.wireOp",EDGE,"E67")])]})]});}
            var Q5;
            Q5=makeQuery(id+"F8.boolean.opBoolean","INTERSECT",EDGE,{"disambiguationData":[OD(0.0)],"derivedFrom":[makeQuery(id+"F5.opExtrude","SWEPT_FACE",FACE,{"disambiguationData":[OSD([sQuery(id+"F4.wireOp",EDGE,"E30")])]}),makeQuery(id+"F8.opExtrude","SWEPT_FACE",FACE,{"disambiguationData":[OSD([sQuery(id+"F7.wireOp",EDGE,"E67")])]})]});
            fillet(context, id + "F14", {"entities" : qUnion([Q0, Q1, Q2, Q3, Q4, Q5]), "radius" : 3 * mm, "tangentPropagation" : true, "allowEdgeOverflow" : false});
        }
        {
            var Q0;
            Q0=makeQuery(id+"F1.opExtrude","CAP_EDGE",EDGE,{"disambiguationData":[OSD([sQuery(id+"F0.wireOp",EDGE,"E1.bottom")])],"isStart":false});
            fillet(context, id + "F15", {"entities" : qUnion([Q0]), "radius" : 2 * mm, "tangentPropagation" : true, "allowEdgeOverflow" : false});
        }
        {
            var Q0;
            Q0=qCreatedBy(makeId("Top.planeOp"),FACE);
            var sketch = newSketch(context, id + "F16", { "sketchPlane" : qUnion([Q0])});
            skLineSegment(sketch, "E79.0", {"start": v(14.05, 38.38) * mm, "end": v(14.05, 198.38) * mm});
            skArc(sketch, "E79.1", {"start": v(24.05, 208.38) * mm, "mid": v(16.98, 205.45) * mm, "end": v(14.05, 198.38) * mm});
            skCircle(sketch, "E79.2", {"center": v(34.05, 185.88) * mm, "radius": 4 * mm});
            skArc(sketch, "E79.3", {"start": v(37.9, 166.56) * mm, "mid": v(35.06, 163.06) * mm, "end": v(34.05, 158.68) * mm});
            skLineSegment(sketch, "E79.4", {"start": v(34.05, 158.68) * mm, "end": v(34.05, 78.09) * mm});
            skArc(sketch, "E79.5", {"start": v(150.2, 166.56) * mm, "mid": v(94.05, 185.88) * mm, "end": v(37.9, 166.56) * mm});
            skLineSegment(sketch, "E79.6", {"start": v(24.05, 208.38) * mm, "end": v(164.05, 208.38) * mm});
            skArc(sketch, "E79.7", {"start": v(174.05, 198.38) * mm, "mid": v(171.12, 205.45) * mm, "end": v(164.05, 208.38) * mm});
            skCircle(sketch, "E79.8", {"center": v(154.05, 185.88) * mm, "radius": 4 * mm});
            skArc(sketch, "E79.9", {"start": v(154.05, 158.68) * mm, "mid": v(153.04, 163.06) * mm, "end": v(150.2, 166.56) * mm});
            skLineSegment(sketch, "E79.10", {"start": v(154.05, 158.68) * mm, "end": v(154.05, 78.09) * mm});
            skLineSegment(sketch, "E79.11", {"start": v(174.05, 38.38) * mm, "end": v(174.05, 198.38) * mm});
            skArc(sketch, "E79.12", {"start": v(164.05, 28.38) * mm, "mid": v(171.12, 31.31) * mm, "end": v(174.05, 38.38) * mm});
            skCircle(sketch, "E79.13", {"center": v(154.05, 50.88) * mm, "radius": 4 * mm});
            skArc(sketch, "E79.14", {"start": v(150.2, 70.2) * mm, "mid": v(153.04, 73.7) * mm, "end": v(154.05, 78.09) * mm});
            skArc(sketch, "E79.15", {"start": v(37.9, 70.2) * mm, "mid": v(94.05, 50.88) * mm, "end": v(150.2, 70.2) * mm});
            skLineSegment(sketch, "E79.16", {"start": v(24.05, 28.38) * mm, "end": v(164.05, 28.38) * mm});
            skArc(sketch, "E79.17", {"start": v(14.05, 38.38) * mm, "mid": v(16.98, 31.31) * mm, "end": v(24.05, 28.38) * mm});
            skCircle(sketch, "E79.18", {"center": v(34.05, 50.88) * mm, "radius": 4 * mm});
            skArc(sketch, "E79.19", {"start": v(34.05, 78.09) * mm, "mid": v(35.06, 73.7) * mm, "end": v(37.9, 70.2) * mm});
            skLineSegment(sketch, "E80", {"start": v(94.05, 208.38) * mm, "end": v(94.05, 238.38) * mm, "construction": true});
            skLineSegment(sketch, "E81", {"start": v(61.05, 208.38) * mm, "end": v(79.05, 226.38) * mm});
            skLineSegment(sketch, "E82", {"start": v(79.05, 226.38) * mm, "end": v(79.05, 238.38) * mm});
            skLineSegment(sketch, "E83", {"start": v(127.05, 208.38) * mm, "end": v(109.05, 226.38) * mm});
            skLineSegment(sketch, "E84", {"start": v(109.05, 226.38) * mm, "end": v(109.05, 238.38) * mm});
            skCircle(sketch, "E85", {"center": v(94.05, 238.38) * mm, "radius": 6 * mm});
            skArc(sketch, "E86", {"start": v(109.05, 238.38) * mm, "mid": v(94.05, 253.38) * mm, "end": v(79.05, 238.38) * mm});
            skLineSegment(sketch, "E87", {"start": v(14.05, 118.38) * mm, "end": v(174.05, 118.38) * mm, "construction": true});
            skArc(sketch, "E88.MirrorCS", {"start": v(109.05, -1.62) * mm, "mid": v(94.05, -16.62) * mm, "end": v(79.05, -1.62) * mm});
            skLineSegment(sketch, "E89.MirrorCS", {"start": v(109.05, 10.38) * mm, "end": v(109.05, -1.62) * mm});
            skCircle(sketch, "E90.MirrorC", {"center": v(94.05, -1.62) * mm, "radius": 6 * mm});
            skLineSegment(sketch, "E91.MirrorCS", {"start": v(79.05, 10.38) * mm, "end": v(79.05, -1.62) * mm});
            skLineSegment(sketch, "E92.MirrorCS", {"start": v(127.05, 28.38) * mm, "end": v(109.05, 10.38) * mm});
            skLineSegment(sketch, "E93.MirrorCS", {"start": v(94.05, 28.38) * mm, "end": v(94.05, -1.62) * mm, "construction": true});
            skLineSegment(sketch, "E94.MirrorCS", {"start": v(61.05, 28.38) * mm, "end": v(79.05, 10.38) * mm});
            skSolve(sketch);
        }
        {
            var Q0;
            Q0=qSketchRegion(id+"F16",true);
            var Q1;
            Q1=makeQuery(id+"F2.opExtrude","CAP_FACE",FACE,{"disambiguationData":[OSD([sQuery(id+"F0.wireOp",EDGE,"E12"),sQuery(id+"F0.wireOp",EDGE,"E13"),sQuery(id+"F0.wireOp",EDGE,"E14"),sQuery(id+"F0.wireOp",EDGE,"E15"),sQuery(id+"F0.wireOp",EDGE,"E17.filletArc"),sQuery(id+"F0.wireOp",EDGE,"E18.filletArc"),sQuery(id+"F0.wireOp",EDGE,"E19.filletArc"),sQuery(id+"F0.wireOp",EDGE,"E20.filletArc"),sQuery(id+"F0.wireOp",EDGE,"E25.0"),sQuery(id+"F0.wireOp",EDGE,"E25.1"),sQuery(id+"F0.wireOp",EDGE,"E25.2"),sQuery(id+"F0.wireOp",EDGE,"E25.3"),sQuery(id+"F0.wireOp",EDGE,"E25.4"),sQuery(id+"F0.wireOp",EDGE,"E25.5"),sQuery(id+"F0.wireOp",EDGE,"E25.6"),sQuery(id+"F0.wireOp",EDGE,"E25.7")])],"isStart":false});
            extrude(context, id + "F17", {"entities" : qUnion([Q0]), "endBound" : BoundingType.UP_TO_SURFACE, "endBoundEntityFace" : qUnion([Q1]), "depth" : 25 * mm});
        }
    });
